# Revit family: Layout-Teknion-Zones_Workshop_Tables_04-R2015
name_source: partatom
category: Furniture Systems
revit_build: Autodesk Revit Architecture 2015 (Build: 20140323_1530(x64)
units: mm (PartAtom-declared; Revit-internal decimal feet)

## types (1)
- Workshop Table 04
    Apparent Load = 21 VA
    Apparent Load Note = Complete With Workshop Table Type Information
    Assembly Code = E2020200
    Connector Description = Power Connector
    Depth = 97 "
    Description = 13'-0" x 8'-5"
    Height = 31.563 "
    Manufacturer = Teknion
    Manufacturer Fax = 416.661.4586
    Model = Workshop Table 04
    Product Line = Zones
    Product Page URL = http://teknionplanningtool.com
    Series = Zones
    Sustainability Data = http://www.teknion.com
    URL = www.teknion.com
    Unit Weight URL = http://www.teknion.com
    Voltage = 120 V
    Voltage Note = Complete With Workshop Table Type Information
    Warranty = http://www.teknion.com
    Width = 97 "

## geometry (parser evidence)
native form markers: Blend x136, Sweep x34
no freeform markers — native parametric forms only
